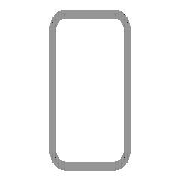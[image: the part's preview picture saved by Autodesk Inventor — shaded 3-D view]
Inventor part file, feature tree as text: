
AUTODESK INVENTOR PART (.ipt)
format: ipt  version: 2025.3 (Build 293356000, 356)  size: 149,504 bytes
history: native  units: mm (DEFAULTED — no unit token found)
features: other x4, plane x3, split x2, sketch x1
ambient origin geometry x8: Origin, YZ Plane, XZ Plane, XY Plane, X Axis, Y Axis, Z Axis, Center Point
bodies: Solid1 (feature_tree), Body (feature_tree)
feature tree (10):
  parser-record x1  (decoder bookkeeping rows leaked as tree rows — omitted from the tree; the rows remain in map.json)
  other  "Driven Length"
  other  "Start Plane"
  other  "End Plane"
  plane  "Work Plane4"
  split  "Split1"
  plane  "Work Plane5"
  split  "Split2"
  sketch  "Sketch3"  dims[d3=994.526745mm d4=0.0mm d7=6.0mm d9=40.0mm d11=80.0mm d12=3.0mm d13=155.186234mm d14=1149.712979mm d15=20.0mm d16=40.0mm d17=90.0deg d18=994.526745mm]
  plane  "Work Plane3"
